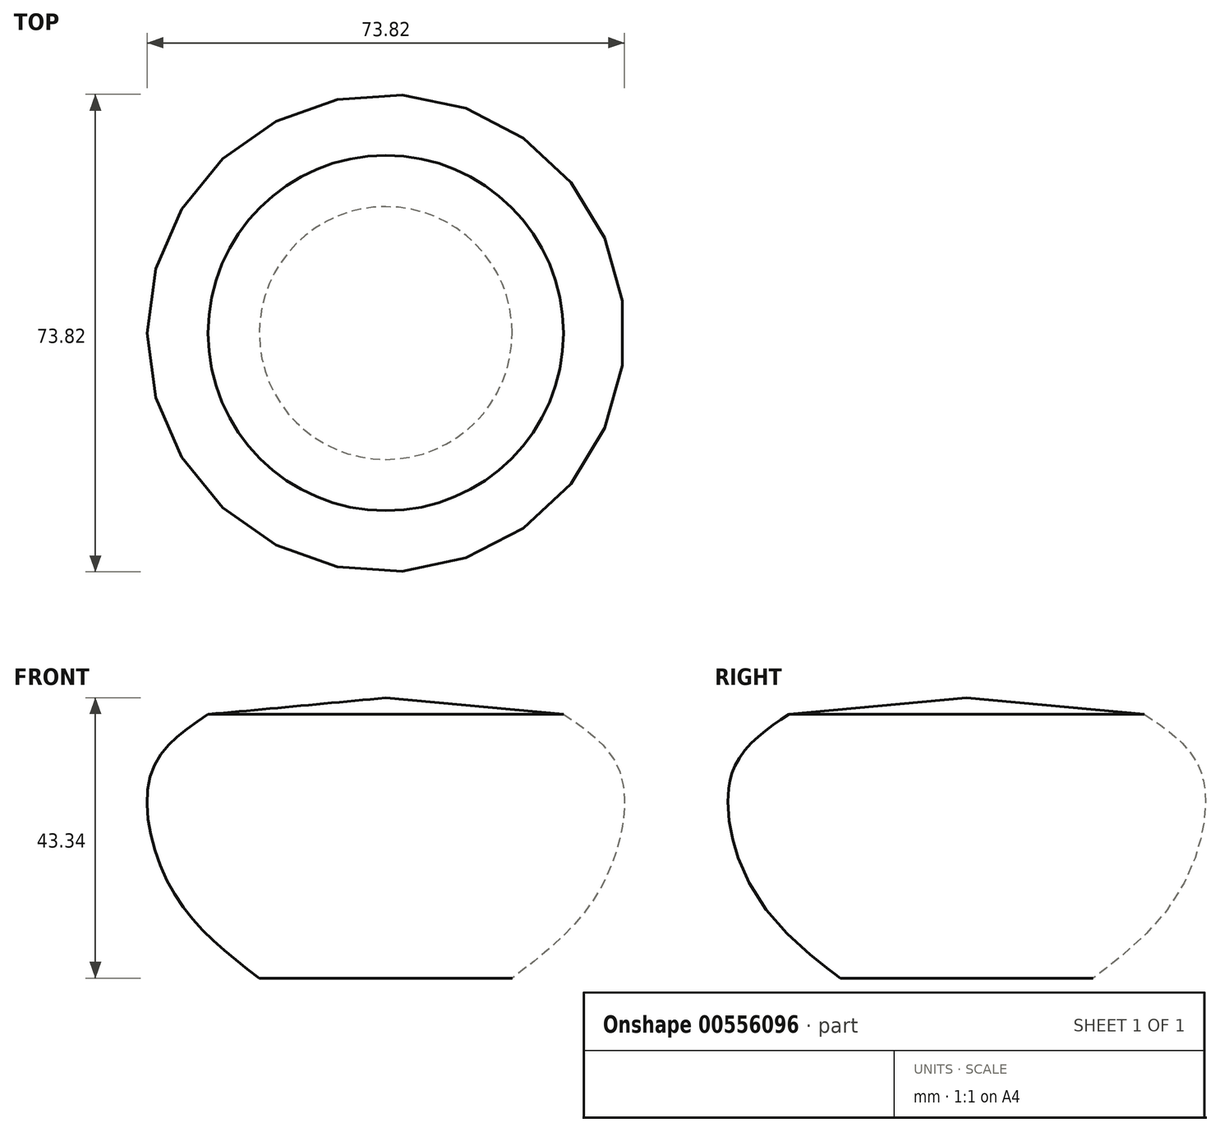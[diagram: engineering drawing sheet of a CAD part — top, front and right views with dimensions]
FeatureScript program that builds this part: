
annotation { "Feature Type Name" : "Feature", "Feature Type Description" : "" }
export const myFeature = defineFeature(function(context is Context, id is Id, definition is map)
    precondition{}
    {
        {
            var Q0;
            Q0=qCreatedBy(makeId("Front.planeOp"),FACE);
            var sketch = newSketch(context, id + "F0", { "sketchPlane" : qUnion([Q0])});
            skLineSegment(sketch, "E0", {"start": v(0, 0) * mm, "end": v(19.55, 0) * mm});
            skFitSpline(sketch, "E1", {"points": [v(19.55, 0) * mm, v(32.86, 13.31) * mm, v(36.26, 31.73) * mm, v(27.48, 40.8) * mm], "startDerivative": vector(42.05, 32.06) * mm, "endDerivative": vector(-38.15, 25.26) * mm});
            skLineSegment(sketch, "E2", {"start": v(0, 0) * mm, "end": v(0, 43.34) * mm});
            skLineSegment(sketch, "E3", {"start": v(0, 43.34) * mm, "end": v(27.48, 40.8) * mm});
            skSolve(sketch);
        }
        {
            var Q0;
            Q0=makeQuery(id+"F0.imprint","IMPRINT",FACE,{"disambiguationData":[TD([[makeQuery(id+"F0.imprint","IMPRINT",EDGE,{"derivedFrom":sQuery(id+"F0.wireOp",EDGE,"E0")}),1.0]])]});
            var Q1;
            Q1=sQuery(id+"F0.wireOp",EDGE,"E2");
            revolve(context, id + "F1", {"entities" : qUnion([Q0]), "axis" : qUnion([Q1]), "revolveType" : RevolveType.FULL});
        }
    });
